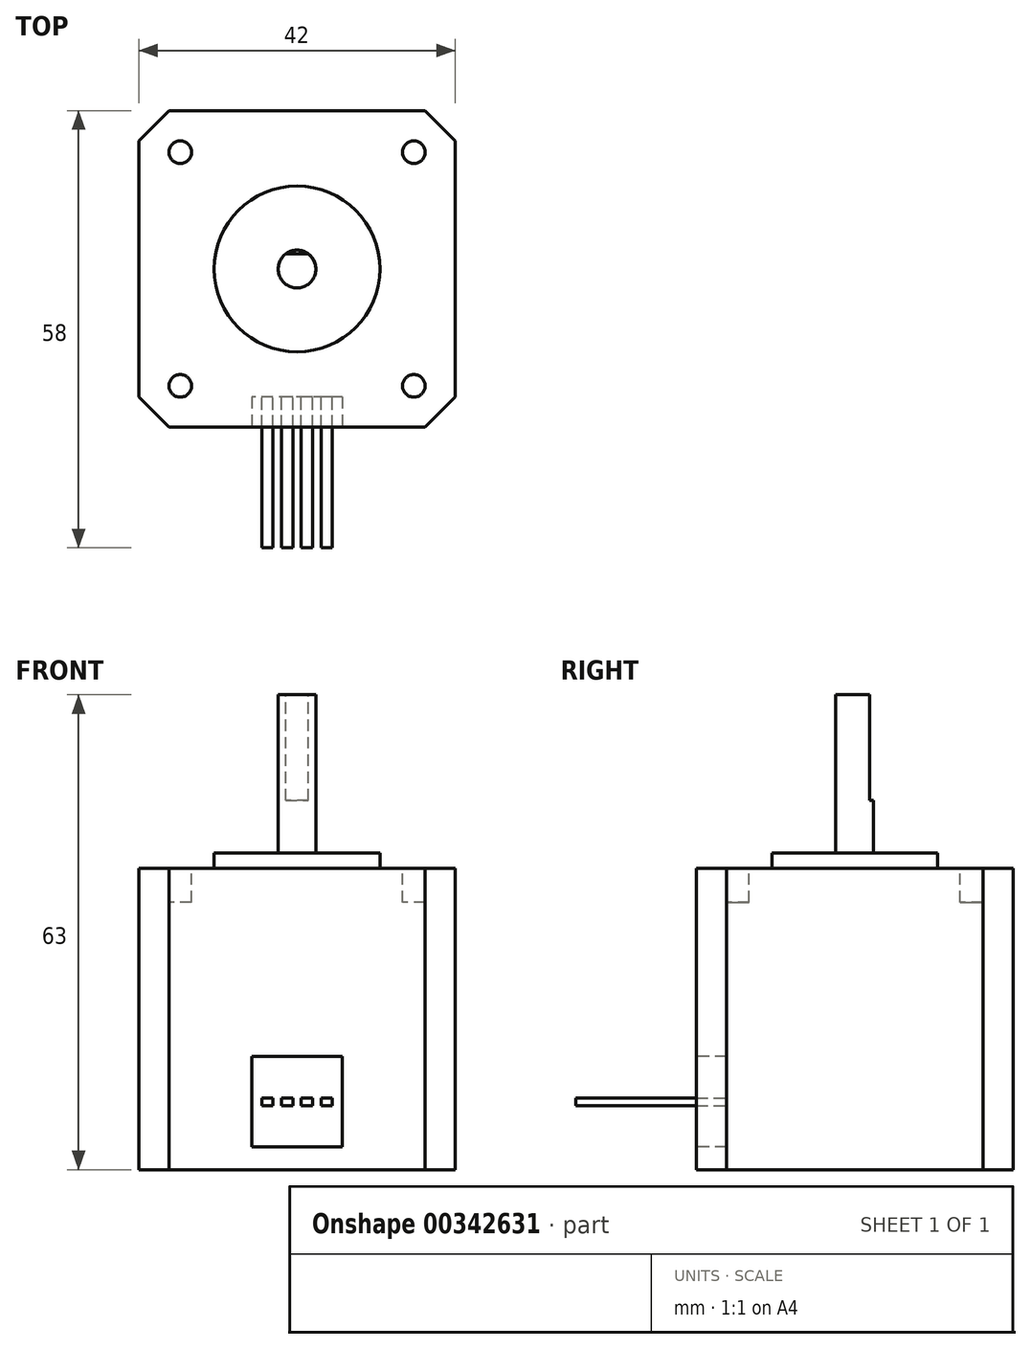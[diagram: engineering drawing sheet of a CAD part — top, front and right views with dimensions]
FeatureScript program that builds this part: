
annotation { "Feature Type Name" : "Feature", "Feature Type Description" : "" }
export const myFeature = defineFeature(function(context is Context, id is Id, definition is map)
    precondition{}
    {
        {
            var Q0;
            Q0=qCreatedBy(makeId("Top.planeOp"),FACE);
            var sketch = newSketch(context, id + "F0", { "sketchPlane" : qUnion([Q0])});
            skLineSegment(sketch, "E0.bottom", {"start": v(21, -21) * mm, "end": v(-21, -21) * mm});
            skLineSegment(sketch, "E0.top", {"start": v(21, 21) * mm, "end": v(-21, 21) * mm});
            skLineSegment(sketch, "E0.left", {"start": v(21, -21) * mm, "end": v(21, 21) * mm});
            skLineSegment(sketch, "E0.right", {"start": v(-21, -21) * mm, "end": v(-21, 21) * mm});
            skPoint(sketch, "E0.middle", {"position": v(0, 0) * mm});
            skSolve(sketch);
        }
        {
            var Q0;
            Q0 = qSketchRegion(id + "F0", true);
            extrude(context, id + "F1", {"entities" : qUnion([Q0]), "depth" : 40 * mm});
        }
        {
            var Q0;
            Q0=makeQuery(id+"F1.opExtrude","CAP_FACE",FACE,{"disambiguationData":[OSD([sQuery(id+"F0.wireOp",EDGE,"E0.bottom"),sQuery(id+"F0.wireOp",EDGE,"E0.top"),sQuery(id+"F0.wireOp",EDGE,"E0.left"),sQuery(id+"F0.wireOp",EDGE,"E0.right")])],"isStart":false});
            var sketch = newSketch(context, id + "F2", { "sketchPlane" : qUnion([Q0])});
            skLineSegment(sketch, "E1", {"start": v(21, -21) * mm, "end": v(-21, 21) * mm, "construction": true});
            skLineSegment(sketch, "E2", {"start": v(-21, -21) * mm, "end": v(21, 21) * mm, "construction": true});
            skCircle(sketch, "E3", {"center": v(15.5, 15.5) * mm, "radius": 1.5 * mm});
            skCircle(sketch, "E4", {"center": v(15.5, -15.5) * mm, "radius": 1.5 * mm});
            skLineSegment(sketch, "E5", {"start": v(15.5, -15.5) * mm, "end": v(15.5, 15.5) * mm, "construction": true});
            skCircle(sketch, "E6.MirrorC", {"center": v(-15.5, -15.5) * mm, "radius": 1.5 * mm});
            skCircle(sketch, "E7.MirrorC", {"center": v(-15.5, 15.5) * mm, "radius": 1.5 * mm});
            skSolve(sketch);
        }
        {
            var Q0;
            Q0 = qSketchRegion(id + "F2", true);
            extrude(context, id + "F3", {"entities" : qUnion([Q0]), "operationType" : NewBodyOperationType.REMOVE, "oppositeDirection" : true, "depth" : 4.5 * mm});
        }
        {
            var Q0;
            Q0=makeQuery(id+"F1.opExtrude","CAP_FACE",FACE,{"disambiguationData":[OSD([sQuery(id+"F0.wireOp",EDGE,"E0.bottom"),sQuery(id+"F0.wireOp",EDGE,"E0.top"),sQuery(id+"F0.wireOp",EDGE,"E0.left"),sQuery(id+"F0.wireOp",EDGE,"E0.right")])],"isStart":false});
            var sketch = newSketch(context, id + "F4", { "sketchPlane" : qUnion([Q0])});
            skLineSegment(sketch, "E8", {"start": v(21, 17) * mm, "end": v(17, 21) * mm});
            skLineSegment(sketch, "E9", {"start": v(15.5, 17) * mm, "end": v(33, 17) * mm, "construction": true});
            skLineSegment(sketch, "E10", {"start": v(21, 17) * mm, "end": v(21, 21) * mm});
            skLineSegment(sketch, "E11", {"start": v(21, 21) * mm, "end": v(17, 21) * mm});
            skLineSegment(sketch, "E12.MirrorCS", {"start": v(21, -21) * mm, "end": v(17, -21) * mm});
            skLineSegment(sketch, "E13.MirrorCS", {"start": v(21, -17) * mm, "end": v(21, -21) * mm});
            skLineSegment(sketch, "E14.MirrorCS", {"start": v(21, -17) * mm, "end": v(17, -21) * mm});
            skLineSegment(sketch, "E15.MirrorCS", {"start": v(-21, -17) * mm, "end": v(-17, -21) * mm});
            skLineSegment(sketch, "E16.MirrorCS", {"start": v(-21, -17) * mm, "end": v(-21, -21) * mm});
            skLineSegment(sketch, "E17.MirrorCS", {"start": v(-21, -21) * mm, "end": v(-17, -21) * mm});
            skLineSegment(sketch, "E18.MirrorCS", {"start": v(-21, 21) * mm, "end": v(-17, 21) * mm});
            skLineSegment(sketch, "E19.MirrorCS", {"start": v(-21, 17) * mm, "end": v(-17, 21) * mm});
            skLineSegment(sketch, "E20.MirrorCS", {"start": v(-21, 17) * mm, "end": v(-21, 21) * mm});
            skSolve(sketch);
        }
        {
            var Q0;
            Q0 = qSketchRegion(id + "F4", true);
            extrude(context, id + "F5", {"entities" : qUnion([Q0]), "operationType" : NewBodyOperationType.REMOVE, "endBound" : BoundingType.THROUGH_ALL, "oppositeDirection" : true, "depth" : 25 * mm});
        }
        {
            var Q0;
            Q0=makeQuery(id+"F1.opExtrude","CAP_FACE",FACE,{"disambiguationData":[OSD([sQuery(id+"F0.wireOp",EDGE,"E0.bottom"),sQuery(id+"F0.wireOp",EDGE,"E0.top"),sQuery(id+"F0.wireOp",EDGE,"E0.left"),sQuery(id+"F0.wireOp",EDGE,"E0.right")])],"isStart":false});
            var sketch = newSketch(context, id + "F6", { "sketchPlane" : qUnion([Q0])});
            skCircle(sketch, "E21", {"center": v(0, 0) * mm, "radius": 11 * mm});
            skSolve(sketch);
        }
        {
            var Q0;
            Q0 = qSketchRegion(id + "F6", true);
            extrude(context, id + "F7", {"entities" : qUnion([Q0]), "operationType" : NewBodyOperationType.ADD, "depth" : 2 * mm});
        }
        {
            var Q0;
            Q0=makeQuery(id+"F7.opExtrude","CAP_FACE",FACE,{"disambiguationData":[OSD([sQuery(id+"F6.wireOp",EDGE,"E21")])],"isStart":false});
            var sketch = newSketch(context, id + "F8", { "sketchPlane" : qUnion([Q0])});
            skCircle(sketch, "E22", {"center": v(0, 0) * mm, "radius": 2.5 * mm});
            skSolve(sketch);
        }
        {
            var Q0;
            Q0 = qSketchRegion(id + "F8", true);
            extrude(context, id + "F9", {"entities" : qUnion([Q0]), "operationType" : NewBodyOperationType.ADD, "depth" : (23 - 2) * mm});
        }
        {
            var Q0;
            Q0=makeQuery(id+"F9.opExtrude","CAP_FACE",FACE,{"disambiguationData":[OSD([sQuery(id+"F8.wireOp",EDGE,"E22")])],"isStart":false});
            var sketch = newSketch(context, id + "F10", { "sketchPlane" : qUnion([Q0])});
            skArc(sketch, "E23.0", {"start": v(1.5, 2) * mm, "mid": v(0, 2.5) * mm, "end": v(-1.5, 2) * mm});
            skLineSegment(sketch, "E24", {"start": v(-1.5, 2) * mm, "end": v(1.5, 2) * mm});
            skSolve(sketch);
        }
        {
            var Q0;
            Q0 = qSketchRegion(id + "F10", true);
            extrude(context, id + "F11", {"entities" : qUnion([Q0]), "operationType" : NewBodyOperationType.REMOVE, "oppositeDirection" : true, "depth" : 14 * mm});
        }
        {
            var Q0;
            Q0=makeQuery(id+"F1.opExtrude","SWEPT_FACE",FACE,{"disambiguationData":[OSD([sQuery(id+"F0.wireOp",EDGE,"E0.bottom")])]});
            var sketch = newSketch(context, id + "F12", { "sketchPlane" : qUnion([Q0])});
            skLineSegment(sketch, "E25.bottom", {"start": v(6, 3) * mm, "end": v(-6, 3) * mm});
            skLineSegment(sketch, "E25.top", {"start": v(6, 15) * mm, "end": v(-6, 15) * mm});
            skLineSegment(sketch, "E25.left", {"start": v(6, 3) * mm, "end": v(6, 15) * mm});
            skLineSegment(sketch, "E25.right", {"start": v(-6, 3) * mm, "end": v(-6, 15) * mm});
            skPoint(sketch, "E25.middle", {"position": v(0, 9) * mm});
            skSolve(sketch);
        }
        {
            var Q0;
            Q0 = qSketchRegion(id + "F12", true);
            extrude(context, id + "F13", {"entities" : qUnion([Q0]), "operationType" : NewBodyOperationType.REMOVE, "oppositeDirection" : true, "depth" : 4 * mm});
        }
        {
            var Q0;
            Q0=makeQuery(id+"F13.boolean.opBoolean","COPY",FACE,{"derivedFrom":makeQuery(id+"F13.opExtrude","CAP_FACE",FACE,{"disambiguationData":[OSD([sQuery(id+"F12.wireOp",EDGE,"E25.bottom"),sQuery(id+"F12.wireOp",EDGE,"E25.top"),sQuery(id+"F12.wireOp",EDGE,"E25.left"),sQuery(id+"F12.wireOp",EDGE,"E25.right")])],"isStart":false})});
            var sketch = newSketch(context, id + "F14", { "sketchPlane" : qUnion([Q0])});
            skLineSegment(sketch, "E26", {"start": v(6, 9) * mm, "end": v(-6, 9) * mm, "construction": true});
            skLineSegment(sketch, "E27.bottom", {"start": v(-3.19, 8.5) * mm, "end": v(-4.69, 8.5) * mm});
            skLineSegment(sketch, "E27.top", {"start": v(-3.19, 9.5) * mm, "end": v(-4.69, 9.5) * mm});
            skLineSegment(sketch, "E27.left", {"start": v(-3.19, 8.5) * mm, "end": v(-3.19, 9.5) * mm});
            skLineSegment(sketch, "E27.right", {"start": v(-4.69, 8.5) * mm, "end": v(-4.69, 9.5) * mm});
            skPoint(sketch, "E27.middle", {"position": v(-3.94, 9) * mm});
            skPoint(sketch, "E28.1.0.0", {"position": v(-1.31, 9) * mm});
            skLineSegment(sketch, "E28.1.0.1", {"start": v(-2.06, 8.5) * mm, "end": v(-2.06, 9.5) * mm});
            skLineSegment(sketch, "E28.1.0.2", {"start": v(-0.56, 8.5) * mm, "end": v(-0.56, 9.5) * mm});
            skLineSegment(sketch, "E28.1.0.3", {"start": v(-0.56, 9.5) * mm, "end": v(-2.06, 9.5) * mm});
            skLineSegment(sketch, "E28.1.0.4", {"start": v(-0.56, 8.5) * mm, "end": v(-2.06, 8.5) * mm});
            skPoint(sketch, "E28.2.0.0", {"position": v(1.31, 9) * mm});
            skLineSegment(sketch, "E28.2.0.1", {"start": v(0.56, 8.5) * mm, "end": v(0.56, 9.5) * mm});
            skLineSegment(sketch, "E28.2.0.2", {"start": v(2.06, 8.5) * mm, "end": v(2.06, 9.5) * mm});
            skLineSegment(sketch, "E28.2.0.3", {"start": v(2.06, 9.5) * mm, "end": v(0.56, 9.5) * mm});
            skLineSegment(sketch, "E28.2.0.4", {"start": v(2.06, 8.5) * mm, "end": v(0.56, 8.5) * mm});
            skPoint(sketch, "E28.3.0.0", {"position": v(3.94, 9) * mm});
            skLineSegment(sketch, "E28.3.0.1", {"start": v(3.19, 8.5) * mm, "end": v(3.19, 9.5) * mm});
            skLineSegment(sketch, "E28.3.0.2", {"start": v(4.69, 8.5) * mm, "end": v(4.69, 9.5) * mm});
            skLineSegment(sketch, "E28.3.0.3", {"start": v(4.69, 9.5) * mm, "end": v(3.19, 9.5) * mm});
            skLineSegment(sketch, "E28.3.0.4", {"start": v(4.69, 8.5) * mm, "end": v(3.19, 8.5) * mm});
            skLineSegment(sketch, "E28.direction1", {"start": v(-3.94, 9) * mm, "end": v(-1.31, 9) * mm, "construction": true});
            skSolve(sketch);
        }
        {
            var Q0;
            Q0 = qSketchRegion(id + "F14", true);
            extrude(context, id + "F15", {"entities" : qUnion([Q0]), "operationType" : NewBodyOperationType.ADD, "depth" : 20 * mm});
        }
    });
